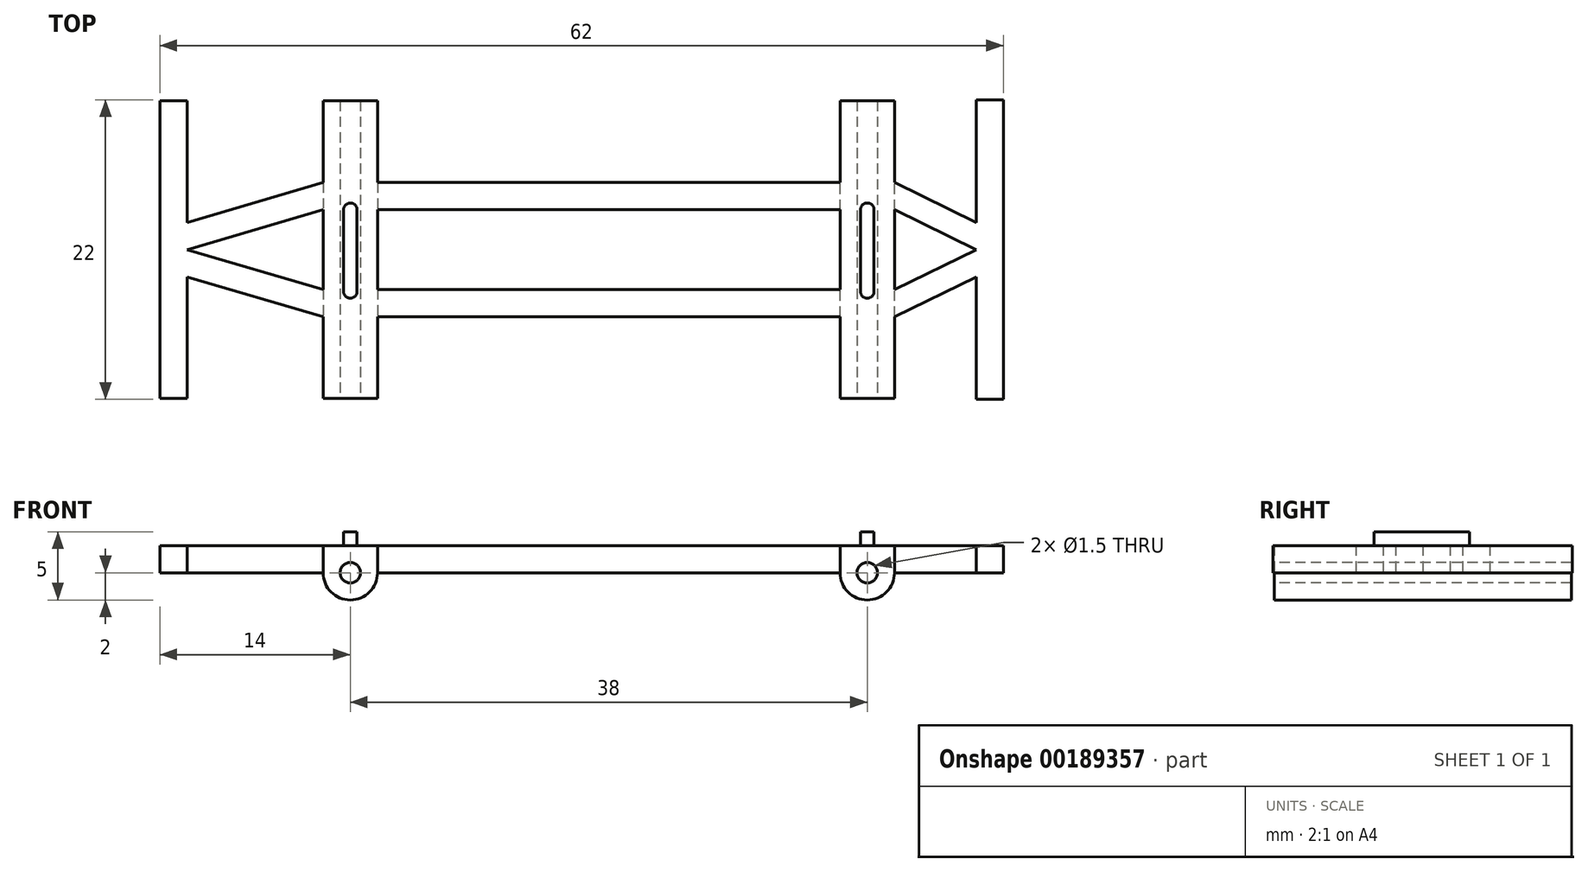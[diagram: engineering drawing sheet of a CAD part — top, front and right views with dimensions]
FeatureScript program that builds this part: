
annotation { "Feature Type Name" : "Feature", "Feature Type Description" : "" }
export const myFeature = defineFeature(function(context is Context, id is Id, definition is map)
    precondition{}
    {
        {
            var Q0;
            Q0=qCreatedBy(makeId("Top.planeOp"),FACE);
            var sketch = newSketch(context, id + "F0", { "sketchPlane" : qUnion([Q0])});
            skLineSegment(sketch, "E0", {"start": v(0, 0) * mm, "end": v(0, -11) * mm});
            skLineSegment(sketch, "E1", {"start": v(0, -11) * mm, "end": v(-2, -11) * mm});
            skLineSegment(sketch, "E2", {"start": v(-2, -11) * mm, "end": v(-2, -2) * mm});
            skLineSegment(sketch, "E3", {"start": v(-2, -2) * mm, "end": v(-8, -4.92) * mm});
            skLineSegment(sketch, "E4", {"start": v(-2, 0) * mm, "end": v(-8, -2.92) * mm});
            skLineSegment(sketch, "E5", {"start": v(-68.75, 0) * mm, "end": v(-12, 0) * mm, "construction": true});
            skLineSegment(sketch, "E6.top", {"start": v(-12, -10.92) * mm, "end": v(-8, -10.92) * mm});
            skLineSegment(sketch, "E6.left", {"start": v(-12, 0) * mm, "end": v(-12, -2.92) * mm});
            skLineSegment(sketch, "E6.right", {"start": v(-8, 0) * mm, "end": v(-8, -2.92) * mm});
            skLineSegment(sketch, "E7.trimOffspring", {"start": v(-8, -4.92) * mm, "end": v(-8, -10.92) * mm});
            skLineSegment(sketch, "E8.trimOffspring", {"start": v(-8, 0) * mm, "end": v(76.35, 0) * mm, "construction": true});
            skLineSegment(sketch, "E9", {"start": v(-12, -2.92) * mm, "end": v(-29, -2.92) * mm});
            skLineSegment(sketch, "E10", {"start": v(-12, -4.92) * mm, "end": v(-29, -4.92) * mm});
            skPoint(sketch, "E10.startSnap0", {"position": v(-12, -5.46) * mm});
            skLineSegment(sketch, "E11", {"start": v(-29, 42.65) * mm, "end": v(-29, -65.17) * mm, "construction": true});
            skLineSegment(sketch, "E12.MirrorCS", {"start": v(-12, 4.92) * mm, "end": v(-29, 4.92) * mm});
            skLineSegment(sketch, "E13.MirrorCS", {"start": v(-12, 2.92) * mm, "end": v(-29, 2.92) * mm});
            skLineSegment(sketch, "E14.MirrorCS", {"start": v(-12, 0) * mm, "end": v(-12, 2.92) * mm});
            skLineSegment(sketch, "E15.MirrorCS", {"start": v(-8, 0) * mm, "end": v(-8, 2.92) * mm});
            skLineSegment(sketch, "E16.MirrorCS", {"start": v(-8, 4.92) * mm, "end": v(-8, 10.92) * mm});
            skLineSegment(sketch, "E17.MirrorCS", {"start": v(-12, 10.92) * mm, "end": v(-8, 10.92) * mm});
            skLineSegment(sketch, "E18.MirrorCS", {"start": v(-2, 2) * mm, "end": v(-8, 4.92) * mm});
            skLineSegment(sketch, "E19.MirrorCS", {"start": v(-2, 0) * mm, "end": v(-8, 2.92) * mm});
            skLineSegment(sketch, "E20.MirrorCS", {"start": v(-2, 11) * mm, "end": v(-2, 2) * mm});
            skLineSegment(sketch, "E21.MirrorCS", {"start": v(0, 11) * mm, "end": v(-2, 11) * mm});
            skLineSegment(sketch, "E22.MirrorCS", {"start": v(0, 0) * mm, "end": v(0, 11) * mm});
            skLineSegment(sketch, "E23.trimOffspring", {"start": v(-12, 4.92) * mm, "end": v(-12, 10.92) * mm});
            skLineSegment(sketch, "E24.trimOffspring", {"start": v(-12, -4.92) * mm, "end": v(-12, -10.92) * mm});
            skLineSegment(sketch, "E25.MirrorCS", {"start": v(-46, 4.92) * mm, "end": v(-29, 4.92) * mm});
            skLineSegment(sketch, "E26.MirrorCS", {"start": v(-46, 2.92) * mm, "end": v(-29, 2.92) * mm});
            skLineSegment(sketch, "E27.MirrorCS", {"start": v(-46, -4.92) * mm, "end": v(-29, -4.92) * mm});
            skLineSegment(sketch, "E28.MirrorCS", {"start": v(-46, -2.92) * mm, "end": v(-29, -2.92) * mm});
            skLineSegment(sketch, "E29.MirrorCS", {"start": v(-46, 0) * mm, "end": v(-46, -2.92) * mm});
            skLineSegment(sketch, "E30.MirrorCS", {"start": v(-46, 0) * mm, "end": v(-46, 2.92) * mm});
            skLineSegment(sketch, "E31.MirrorCS", {"start": v(-46, 4.92) * mm, "end": v(-46, 10.92) * mm});
            skLineSegment(sketch, "E32.MirrorCS", {"start": v(-46, 10.92) * mm, "end": v(-50, 10.92) * mm});
            skLineSegment(sketch, "E33.MirrorCS", {"start": v(-50, 4.92) * mm, "end": v(-50, 10.92) * mm});
            skLineSegment(sketch, "E34.MirrorCS", {"start": v(-50, -4.92) * mm, "end": v(-50, -10.92) * mm});
            skLineSegment(sketch, "E35.MirrorCS", {"start": v(-46, -10.92) * mm, "end": v(-50, -10.92) * mm});
            skLineSegment(sketch, "E36.MirrorCS", {"start": v(-46, -4.92) * mm, "end": v(-46, -10.92) * mm});
            skPoint(sketch, "E37.MirrorCS.end.orphan", {"position": v(-50, 4.92) * mm});
            skPoint(sketch, "E38.MirrorCS.end.orphan", {"position": v(-50, -4.92) * mm});
            skLineSegment(sketch, "E39", {"start": v(-60, -2) * mm, "end": v(-60, -10.92) * mm});
            skLineSegment(sketch, "E40", {"start": v(-60, -10.92) * mm, "end": v(-62, -10.92) * mm});
            skLineSegment(sketch, "E41", {"start": v(-62, -10.92) * mm, "end": v(-62, 10.92) * mm});
            skLineSegment(sketch, "E42", {"start": v(-62, 10.92) * mm, "end": v(-60, 10.92) * mm});
            skLineSegment(sketch, "E43", {"start": v(-60, 10.92) * mm, "end": v(-60, 2) * mm});
            skLineSegment(sketch, "E44", {"start": v(-50, -4.92) * mm, "end": v(-60, -2) * mm});
            skLineSegment(sketch, "E45", {"start": v(-50, 4.92) * mm, "end": v(-60, 2) * mm});
            skPoint(sketch, "E46.startSnap0", {"position": v(-55, 3.46) * mm});
            skPoint(sketch, "E46.endSnap0", {"position": v(-55, -3.46) * mm});
            skLineSegment(sketch, "E47", {"start": v(-50, 2.92) * mm, "end": v(-60, 0) * mm});
            skLineSegment(sketch, "E48", {"start": v(-60, 0) * mm, "end": v(-50, -2.92) * mm});
            skLineSegment(sketch, "E49", {"start": v(-50, -2.92) * mm, "end": v(-50, 2.92) * mm});
            skSolve(sketch);
        }
        {
            var Q0;
            Q0 = qSketchRegion(id + "F0", true);
            extrude(context, id + "F1", {"entities" : qUnion([Q0]), "depth" : 2 * mm});
        }
        {
            var Q0;
            Q0=makeQuery(id+"F1.opExtrude","CAP_FACE",FACE,{"disambiguationData":[OSD([sQuery(id+"F0.wireOp",EDGE,"E0"),sQuery(id+"F0.wireOp",EDGE,"E1"),sQuery(id+"F0.wireOp",EDGE,"E2"),sQuery(id+"F0.wireOp",EDGE,"E3"),sQuery(id+"F0.wireOp",EDGE,"E4"),sQuery(id+"F0.wireOp",EDGE,"E6.top"),sQuery(id+"F0.wireOp",EDGE,"E6.left"),sQuery(id+"F0.wireOp",EDGE,"E6.right"),sQuery(id+"F0.wireOp",EDGE,"E7.trimOffspring"),sQuery(id+"F0.wireOp",EDGE,"E9"),sQuery(id+"F0.wireOp",EDGE,"E10"),sQuery(id+"F0.wireOp",EDGE,"E12.MirrorCS"),sQuery(id+"F0.wireOp",EDGE,"E13.MirrorCS"),sQuery(id+"F0.wireOp",EDGE,"E15.MirrorCS"),sQuery(id+"F0.wireOp",EDGE,"E16.MirrorCS"),sQuery(id+"F0.wireOp",EDGE,"E14.MirrorCS"),sQuery(id+"F0.wireOp",EDGE,"E17.MirrorCS"),sQuery(id+"F0.wireOp",EDGE,"E18.MirrorCS"),sQuery(id+"F0.wireOp",EDGE,"E19.MirrorCS"),sQuery(id+"F0.wireOp",EDGE,"E20.MirrorCS"),sQuery(id+"F0.wireOp",EDGE,"E21.MirrorCS"),sQuery(id+"F0.wireOp",EDGE,"E22.MirrorCS"),sQuery(id+"F0.wireOp",EDGE,"E24.trimOffspring"),sQuery(id+"F0.wireOp",EDGE,"E23.trimOffspring"),sQuery(id+"F0.wireOp",EDGE,"E25.MirrorCS"),sQuery(id+"F0.wireOp",EDGE,"E26.MirrorCS"),sQuery(id+"F0.wireOp",EDGE,"E27.MirrorCS"),sQuery(id+"F0.wireOp",EDGE,"E28.MirrorCS"),sQuery(id+"F0.wireOp",EDGE,"E29.MirrorCS"),sQuery(id+"F0.wireOp",EDGE,"E30.MirrorCS"),sQuery(id+"F0.wireOp",EDGE,"E31.MirrorCS"),sQuery(id+"F0.wireOp",EDGE,"E32.MirrorCS"),sQuery(id+"F0.wireOp",EDGE,"E33.MirrorCS"),sQuery(id+"F0.wireOp",EDGE,"E34.MirrorCS"),sQuery(id+"F0.wireOp",EDGE,"E35.MirrorCS"),sQuery(id+"F0.wireOp",EDGE,"E36.MirrorCS"),sQuery(id+"F0.wireOp",EDGE,"E39"),sQuery(id+"F0.wireOp",EDGE,"E40"),sQuery(id+"F0.wireOp",EDGE,"E41"),sQuery(id+"F0.wireOp",EDGE,"E42"),sQuery(id+"F0.wireOp",EDGE,"E43"),sQuery(id+"F0.wireOp",EDGE,"E44"),sQuery(id+"F0.wireOp",EDGE,"E45"),sQuery(id+"F0.wireOp",EDGE,"E47"),sQuery(id+"F0.wireOp",EDGE,"E48"),sQuery(id+"F0.wireOp",EDGE,"E49")])],"isStart":false});
            var sketch = newSketch(context, id + "F2", { "sketchPlane" : qUnion([Q0])});
            skLineSegment(sketch, "E50", {"start": v(-48, 2.92) * mm, "end": v(-48, -3.08) * mm, "construction": true});
            skPoint(sketch, "E50.startSnap0", {"position": v(-48, 10.92) * mm});
            skArc(sketch, "E51", {"start": v(-47.5, 2.92) * mm, "mid": v(-48, 3.42) * mm, "end": v(-48.5, 2.92) * mm});
            skArc(sketch, "E52", {"start": v(-47.5, -3.08) * mm, "mid": v(-48, -3.58) * mm, "end": v(-48.5, -3.08) * mm});
            skLineSegment(sketch, "E53", {"start": v(-48.5, 2.92) * mm, "end": v(-48.5, -3.08) * mm});
            skLineSegment(sketch, "E54", {"start": v(-47.5, 2.92) * mm, "end": v(-47.5, -3.08) * mm});
            skLineSegment(sketch, "E55", {"start": v(-70.51, 2.92) * mm, "end": v(-48, 2.92) * mm, "construction": true});
            skLineSegment(sketch, "E56", {"start": v(-29, 29.5) * mm, "end": v(-29, -26.1) * mm, "construction": true});
            skPoint(sketch, "E56.startSnap0", {"position": v(-29, 4.92) * mm});
            skLineSegment(sketch, "E57.MirrorCS", {"start": v(-9.5, 2.92) * mm, "end": v(-9.5, -3.08) * mm});
            skLineSegment(sketch, "E58.MirrorCS", {"start": v(-10.5, 2.92) * mm, "end": v(-10.5, -3.08) * mm});
            skArc(sketch, "E59.MirrorCS", {"start": v(-10.5, -3.08) * mm, "mid": v(-10, -3.58) * mm, "end": v(-9.5, -3.08) * mm});
            skArc(sketch, "E60.MirrorCS", {"start": v(-10.5, 2.92) * mm, "mid": v(-10, 3.42) * mm, "end": v(-9.5, 2.92) * mm});
            skLineSegment(sketch, "E61.MirrorCS", {"start": v(-10, 2.92) * mm, "end": v(-10, -3.08) * mm, "construction": true});
            skSolve(sketch);
        }
        {
            var Q0;
            Q0 = qSketchRegion(id + "F2", true);
            extrude(context, id + "F3", {"entities" : qUnion([Q0]), "operationType" : NewBodyOperationType.ADD, "depth" : 1 * mm});
        }
        {
            var Q0;
            Q0=makeQuery(id+"F1.opExtrude","SWEPT_FACE",FACE,{"disambiguationData":[OSD([sQuery(id+"F0.wireOp",EDGE,"E35.MirrorCS")])]});
            var sketch = newSketch(context, id + "F4", { "sketchPlane" : qUnion([Q0])});
            skArc(sketch, "E62", {"start": v(-50, 0) * mm, "mid": v(-48, -2) * mm, "end": v(-46, 0) * mm});
            skLineSegment(sketch, "E63", {"start": v(-50, 0) * mm, "end": v(-46, 0) * mm});
            skSolve(sketch);
        }
        {
            var Q0;
            Q0 = qSketchRegion(id + "F4", true);
            var Q1;
            Q1=makeQuery(id+"F1.opExtrude","SWEPT_FACE",FACE,{"disambiguationData":[OSD([sQuery(id+"F0.wireOp",EDGE,"E32.MirrorCS")])]});
            extrude(context, id + "F5", {"entities" : qUnion([Q0]), "operationType" : NewBodyOperationType.ADD, "endBound" : BoundingType.UP_TO_SURFACE, "oppositeDirection" : true, "endBoundEntityFace" : qUnion([Q1]), "depth" : 25 * mm});
        }
        {
            var Q0;
            {var subQ0=sQuery(id+"F0.wireOp",EDGE,"E23.trimOffspring");var subQ1=sQuery(id+"F0.wireOp",EDGE,"E26.MirrorCS");var subQ2=sQuery(id+"F0.wireOp",EDGE,"E13.MirrorCS");var subQ3=sQuery(id+"F0.wireOp",EDGE,"E16.MirrorCS");var subQ4=sQuery(id+"F0.wireOp",EDGE,"E24.trimOffspring");var subQ5=sQuery(id+"F0.wireOp",EDGE,"E30.MirrorCS");var subQ6=sQuery(id+"F0.wireOp",EDGE,"E29.MirrorCS");var subQ7=sQuery(id+"F0.wireOp",EDGE,"E27.MirrorCS");var subQ8=sQuery(id+"F0.wireOp",EDGE,"E10");var subQ9=sQuery(id+"F0.wireOp",EDGE,"E21.MirrorCS");var subQ10=sQuery(id+"F0.wireOp",EDGE,"E3");var subQ11=sQuery(id+"F0.wireOp",EDGE,"E2");var subQ12=sQuery(id+"F0.wireOp",EDGE,"E1");var subQ13=sQuery(id+"F0.wireOp",EDGE,"E18.MirrorCS");var subQ14=sQuery(id+"F0.wireOp",EDGE,"E20.MirrorCS");var subQ15=sQuery(id+"F0.wireOp",EDGE,"E7.trimOffspring");var subQ16=sQuery(id+"F0.wireOp",EDGE,"E19.MirrorCS");var subQ17=sQuery(id+"F0.wireOp",EDGE,"E25.MirrorCS");var subQ18=sQuery(id+"F0.wireOp",EDGE,"E12.MirrorCS");var subQ19=sQuery(id+"F0.wireOp",EDGE,"E22.MirrorCS");var subQ20=sQuery(id+"F0.wireOp",EDGE,"E0");var subQ21=sQuery(id+"F0.wireOp",EDGE,"E4");var subQ22=sQuery(id+"F0.wireOp",EDGE,"E6.top");var subQ23=sQuery(id+"F0.wireOp",EDGE,"E14.MirrorCS");var subQ24=sQuery(id+"F0.wireOp",EDGE,"E6.left");var subQ25=sQuery(id+"F0.wireOp",EDGE,"E17.MirrorCS");var subQ26=sQuery(id+"F0.wireOp",EDGE,"E15.MirrorCS");var subQ27=sQuery(id+"F0.wireOp",EDGE,"E6.right");var subQ28=sQuery(id+"F0.wireOp",EDGE,"E28.MirrorCS");var subQ29=sQuery(id+"F0.wireOp",EDGE,"E9");var subQ30=sQuery(id+"F0.wireOp",EDGE,"E31.MirrorCS");var subQ31=sQuery(id+"F0.wireOp",EDGE,"E36.MirrorCS");Q0=makeQuery(id+"F5.boolean.opBoolean","SPLIT",FACE,{"disambiguationData":[TD([makeQuery(id+"F1.opExtrude","SWEPT_FACE",FACE,{"disambiguationData":[OSD([subQ12])]})])],"derivedFrom":makeQuery(id+"F1.opExtrude","CAP_FACE",FACE,{"disambiguationData":[OSD([subQ20,subQ12,subQ11,subQ10,subQ21,subQ22,subQ24,subQ27,subQ15,subQ29,subQ8,subQ18,subQ2,subQ26,subQ3,subQ23,subQ25,subQ13,subQ16,subQ14,subQ9,subQ19,subQ4,subQ0,subQ17,subQ1,subQ7,subQ28,subQ6,subQ5,subQ30,sQuery(id+"F0.wireOp",EDGE,"E32.MirrorCS"),sQuery(id+"F0.wireOp",EDGE,"E33.MirrorCS"),sQuery(id+"F0.wireOp",EDGE,"E34.MirrorCS"),sQuery(id+"F0.wireOp",EDGE,"E35.MirrorCS"),subQ31,sQuery(id+"F0.wireOp",EDGE,"E39"),sQuery(id+"F0.wireOp",EDGE,"E40"),sQuery(id+"F0.wireOp",EDGE,"E41"),sQuery(id+"F0.wireOp",EDGE,"E42"),sQuery(id+"F0.wireOp",EDGE,"E43"),sQuery(id+"F0.wireOp",EDGE,"E44"),sQuery(id+"F0.wireOp",EDGE,"E45"),sQuery(id+"F0.wireOp",EDGE,"E47"),sQuery(id+"F0.wireOp",EDGE,"E48"),sQuery(id+"F0.wireOp",EDGE,"E49")])],"isStart":true})});}
            var sketch = newSketch(context, id + "F6", { "sketchPlane" : qUnion([Q0])});
            skLineSegment(sketch, "E64.bottom", {"start": v(-12, 10.92) * mm, "end": v(-8, 10.92) * mm});
            skLineSegment(sketch, "E64.top", {"start": v(-12, -10.92) * mm, "end": v(-8, -10.92) * mm});
            skLineSegment(sketch, "E64.left", {"start": v(-12, 10.92) * mm, "end": v(-12, -10.92) * mm});
            skLineSegment(sketch, "E64.right", {"start": v(-8, 10.92) * mm, "end": v(-8, -10.92) * mm});
            skSolve(sketch);
        }
        {
            var Q0;
            Q0 = qSketchRegion(id + "F6", true);
            extrude(context, id + "F7", {"entities" : qUnion([Q0]), "operationType" : NewBodyOperationType.ADD, "depth" : 2 * mm});
        }
        {
            var Q0;
            Q0=makeQuery(id+"F7.opExtrude","CAP_EDGE",EDGE,{"disambiguationData":[OSD([sQuery(id+"F6.wireOp",EDGE,"E64.left")])],"isStart":false});
            var Q1;
            Q1=makeQuery(id+"F7.opExtrude","CAP_EDGE",EDGE,{"disambiguationData":[OSD([sQuery(id+"F6.wireOp",EDGE,"E64.right")])],"isStart":false});
            fillet(context, id + "F8", {"entities" : qUnion([Q0, Q1]), "radius" : 2 * mm, "tangentPropagation" : true, "allowEdgeOverflow" : false});
        }
        {
            var Q0;
            Q0=makeQuery(id+"F5.boolean.opBoolean","MERGE",FACE,{"derivedFrom":[makeQuery(id+"F1.opExtrude","SWEPT_FACE",FACE,{"disambiguationData":[OSD([sQuery(id+"F0.wireOp",EDGE,"E35.MirrorCS")])]}),makeQuery(id+"F5.opExtrude","CAP_FACE",FACE,{"disambiguationData":[OSD([sQuery(id+"F4.wireOp",EDGE,"E62"),sQuery(id+"F4.wireOp",EDGE,"E63")])],"isStart":true})]});
            var sketch = newSketch(context, id + "F9", { "sketchPlane" : qUnion([Q0])});
            skCircle(sketch, "E65", {"center": v(-48, 0) * mm, "radius": 0.75 * mm});
            skSolve(sketch);
        }
        {
            var Q0;
            Q0=makeQuery(id+"F7.boolean.opBoolean","MERGE",FACE,{"derivedFrom":[makeQuery(id+"F1.opExtrude","SWEPT_FACE",FACE,{"disambiguationData":[OSD([sQuery(id+"F0.wireOp",EDGE,"E6.top")])]}),makeQuery(id+"F7.opExtrude","SWEPT_FACE",FACE,{"disambiguationData":[OSD([sQuery(id+"F6.wireOp",EDGE,"E64.bottom")])]})]});
            var sketch = newSketch(context, id + "F10", { "sketchPlane" : qUnion([Q0])});
            skCircle(sketch, "E66", {"center": v(-10, 0) * mm, "radius": 0.75 * mm});
            skSolve(sketch);
        }
        {
            var Q0;
            Q0 = qSketchRegion(id + "F10", true);
            var Q1;
            Q1=makeQuery(id+"F9.imprint","IMPRINT",FACE,{"disambiguationData":[TD([[makeQuery(id+"F9.imprint","IMPRINT",EDGE,{"derivedFrom":sQuery(id+"F9.wireOp",EDGE,"E65")}),1.0]])]});
            extrude(context, id + "F11", {"entities" : qUnion([Q0, Q1]), "operationType" : NewBodyOperationType.REMOVE, "endBound" : BoundingType.THROUGH_ALL, "oppositeDirection" : true, "depth" : 25 * mm});
        }
    });
